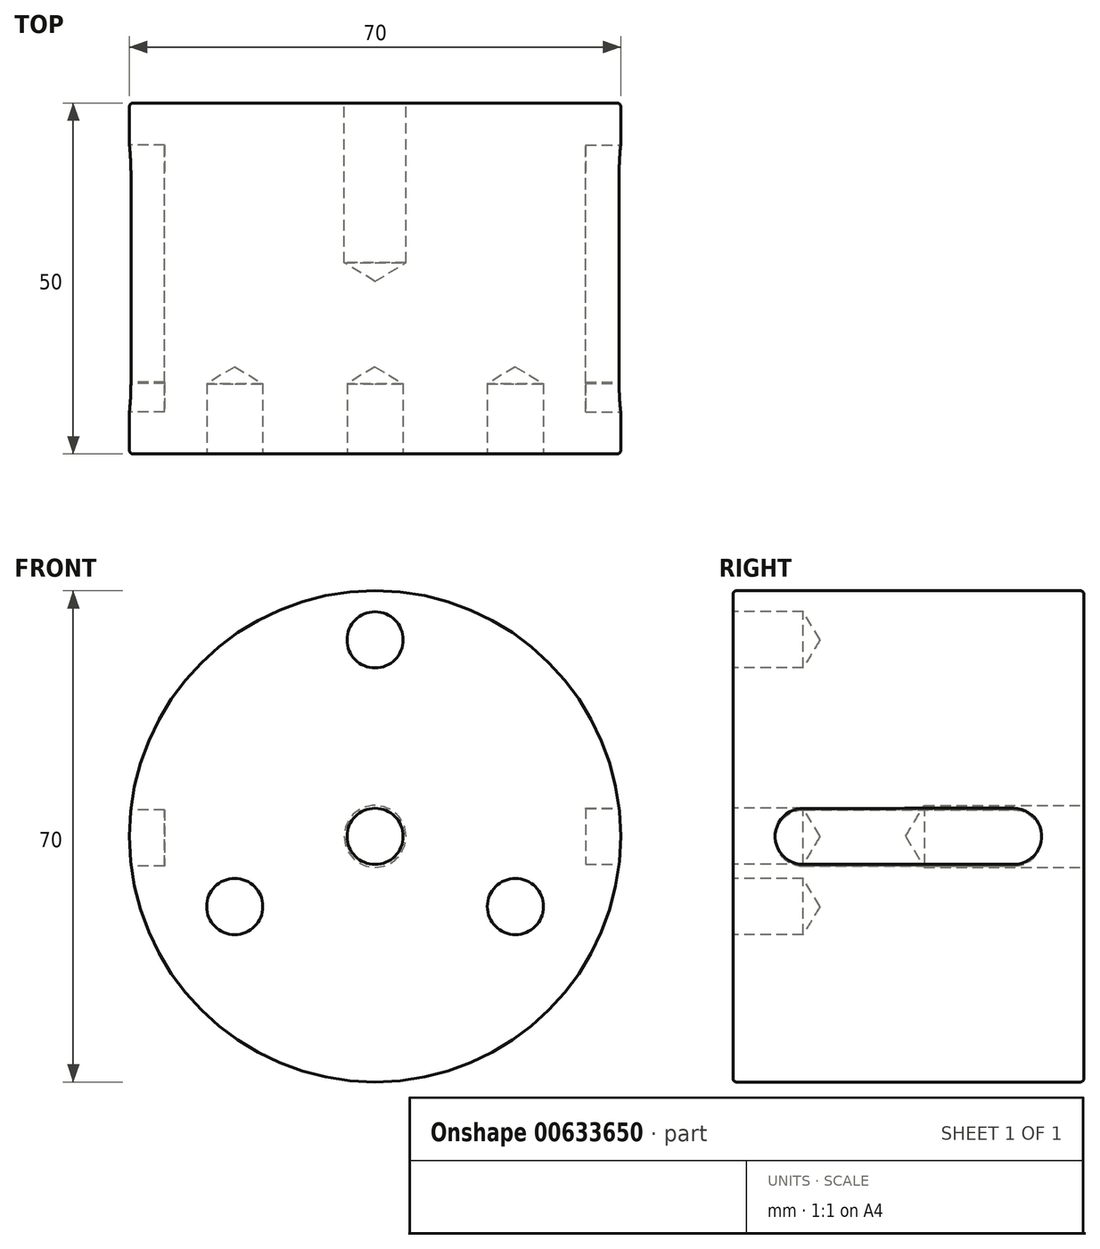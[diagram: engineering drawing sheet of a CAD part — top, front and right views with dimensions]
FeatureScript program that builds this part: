
annotation { "Feature Type Name" : "Feature", "Feature Type Description" : "" }
export const myFeature = defineFeature(function(context is Context, id is Id, definition is map)
    precondition{}
    {
        {
            var Q0;
            Q0=qCreatedBy(makeId("Front.planeOp"),FACE);
            var sketch = newSketch(context, id + "F0", { "sketchPlane" : qUnion([Q0])});
            skCircle(sketch, "E0", {"center": v(0, 0) * mm, "radius": 35 * mm});
            skSolve(sketch);
        }
        {
            var Q0;
            Q0=makeQuery(id+"F0.imprint","IMPRINT",FACE,{"disambiguationData":[TD([[makeQuery(id+"F0.imprint","IMPRINT",EDGE,{"derivedFrom":sQuery(id+"F0.wireOp",EDGE,"E0")}),1.0]])]});
            extrude(context, id + "F1", {"entities" : qUnion([Q0]), "depth" : 50 * mm, "offsetDistance" : 25 * mm});
        }
        {
            var Q0;
            Q0=makeQuery(id+"F1.opExtrude","CAP_FACE",FACE,{"disambiguationData":[OSD([sQuery(id+"F0.wireOp",EDGE,"E0")])],"isStart":false});
            var sketch = newSketch(context, id + "F2", { "sketchPlane" : qUnion([Q0])});
            skPoint(sketch, "E1", {"position": v(0, 28) * mm});
            skPoint(sketch, "E2", {"position": v(0, 0) * mm});
            skPoint(sketch, "E3", {"position": v(-20, -10) * mm});
            skPoint(sketch, "E4", {"position": v(20, -10) * mm});
            skSolve(sketch);
        }
        {
            var Q0;
            Q0=sQuery(id+"F2.wireOp",VERTEX,"E1");
            var Q1;
            Q1=sQuery(id+"F2.wireOp",VERTEX,"E2");
            var Q2;
            Q2=sQuery(id+"F2.wireOp",VERTEX,"E4");
            var Q3;
            Q3=sQuery(id+"F2.wireOp",VERTEX,"E3");
            var Q4;
            Q4=makeQuery(id+"F1.opExtrude","SWEPT_BODY",BODY,{"disambiguationData":[OSD([sQuery(id+"F0.wireOp",EDGE,"E0")])]});
            hole(context, id + "F3", {"style" : HoleStyle.SIMPLE, "endStyle" : HoleEndStyle.BLIND, "holeDiameter" : 8 * mm, "majorDiameter" : 12 * mm, "holeDepth" : 10 * mm, "isTappedThrough" : true, "tappedDepth" : 8 * mm, "tapClearance" : 3, "startFromSketch" : true, "locations" : qUnion([Q0, Q1, Q2, Q3]), "scope" : qUnion([Q4])});
        }
        {
            var Q0;
            Q0=qCreatedBy(makeId("Right.planeOp"),FACE);
            cPlane(context, id + "F4", {"entities" : qUnion([Q0]), "cplaneType" : CPlaneType.OFFSET, "offset" : 35 * mm, "width" : 150 * mm, "height" : 150 * mm});
        }
        {
            var Q0;
            Q0=qCreatedBy(id+"F4.planeOp",FACE);
            var sketch = newSketch(context, id + "F5", { "sketchPlane" : qUnion([Q0])});
            skPoint(sketch, "E5", {"position": v(-40, 0) * mm});
            skPoint(sketch, "E6", {"position": v(-10, 0) * mm});
            skArc(sketch, "E7", {"start": v(-39.76, 4) * mm, "mid": v(-44, 0.1) * mm, "end": v(-39.95, -4) * mm});
            skArc(sketch, "E8", {"start": v(-10, -4) * mm, "mid": v(-6, 0) * mm, "end": v(-10, 4) * mm});
            skLineSegment(sketch, "E9", {"start": v(-39.95, -4) * mm, "end": v(-10, -4) * mm});
            skLineSegment(sketch, "E10", {"start": v(-39.76, 4) * mm, "end": v(-10, 4) * mm});
            skSolve(sketch);
        }
        {
            var Q0;
            Q0 = qSketchRegion(id + "F5", true);
            var Q1;
            Q1=makeQuery(id+"F5.imprint","IMPRINT",FACE,{"disambiguationData":[TD([[makeQuery(id+"F5.imprint","IMPRINT",EDGE,{"derivedFrom":sQuery(id+"F5.wireOp",EDGE,"E7")}),1.0]])]});
            extrude(context, id + "F6", {"entities" : qUnion([Q0, Q1]), "operationType" : NewBodyOperationType.REMOVE, "oppositeDirection" : true, "depth" : 5 * mm, "offsetDistance" : 25 * mm});
        }
        {
            var Q0;
            Q0=qCreatedBy(makeId("Right.planeOp"),FACE);
            cPlane(context, id + "F7", {"entities" : qUnion([Q0]), "cplaneType" : CPlaneType.OFFSET, "offset" : 35 * mm, "oppositeDirection" : true, "width" : 150 * mm, "height" : 150 * mm});
        }
        {
            var Q0;
            Q0=qCreatedBy(id+"F7.planeOp",FACE);
            var sketch = newSketch(context, id + "F8", { "sketchPlane" : qUnion([Q0])});
            skPoint(sketch, "E11", {"position": v(-10, 0) * mm});
            skPoint(sketch, "E12", {"position": v(-40, -0.23) * mm});
            skPoint(sketch, "E13", {"position": v(-10, -0.22) * mm});
            skArc(sketch, "E14", {"start": v(-39.76, 3.76) * mm, "mid": v(-44, -0.14) * mm, "end": v(-39.95, -4.23) * mm});
            skArc(sketch, "E15", {"start": v(-10, -4.22) * mm, "mid": v(-6, -0.22) * mm, "end": v(-10, 3.78) * mm});
            skLineSegment(sketch, "E16", {"start": v(-39.95, -4.23) * mm, "end": v(-10, -4.22) * mm});
            skLineSegment(sketch, "E17", {"start": v(-39.76, 3.76) * mm, "end": v(-10, 3.78) * mm});
            skSolve(sketch);
        }
        {
            var Q0;
            Q0=makeQuery(id+"F8.imprint","IMPRINT",FACE,{"disambiguationData":[TD([[makeQuery(id+"F8.imprint","IMPRINT",EDGE,{"derivedFrom":sQuery(id+"F8.wireOp",EDGE,"E14")}),1.0]])]});
            extrude(context, id + "F9", {"entities" : qUnion([Q0]), "operationType" : NewBodyOperationType.REMOVE, "depth" : 5 * mm, "offsetDistance" : 25 * mm});
        }
        {
            var Q0;
            Q0=qCreatedBy(makeId("Front.planeOp"),FACE);
            var sketch = newSketch(context, id + "F10", { "sketchPlane" : qUnion([Q0])});
            skPoint(sketch, "E18", {"position": v(0, 0) * mm});
            skSolve(sketch);
        }
        {
            var Q0;
            Q0=sQuery(id+"F10.wireOp",VERTEX,"E18");
            var Q1;
            Q1=makeQuery(id+"F1.opExtrude","SWEPT_BODY",BODY,{"disambiguationData":[OSD([sQuery(id+"F0.wireOp",EDGE,"E0")])]});
            hole(context, id + "F11", {"style" : HoleStyle.SIMPLE, "endStyle" : HoleEndStyle.BLIND, "oppositeDirection" : true, "standardTappedOrClearance" : lookupTablePath({ "standard" : "ISO", "engagement" : "75%", "pitch" : "1.25 mm", "size" : "M10", "type" : "Tapped" }), "standardBlindInLast" : lookupTablePath({ "standard" : "ISO", "engagement" : "75%", "pitch" : "1.25 mm", "size" : "M10", "type" : "Tapped" }), "holeDiameter" : 8.8 * mm, "majorDiameter" : 10 * mm, "showTappedDepth" : true, "holeDepth" : 22.75 * mm, "isTappedThrough" : true, "tappedDepth" : 19 * mm, "tapClearance" : 3, "locations" : qUnion([Q0]), "scope" : qUnion([Q1])});
        }
        {
            var Q0;
            Q0=makeQuery(id+"F1.opExtrude","CAP_EDGE",EDGE,{"disambiguationData":[OSD([sQuery(id+"F0.wireOp",EDGE,"E0")])],"isStart":false});
            var Q1;
            Q1=makeQuery(id+"F1.opExtrude","CAP_EDGE",EDGE,{"disambiguationData":[OSD([sQuery(id+"F0.wireOp",EDGE,"E0")])],"isStart":true});
            fillet(context, id + "F12", {"entities" : qUnion([Q0, Q1]), "radius" : .5 * mm, "tangentPropagation" : true, "allowEdgeOverflow" : false});
        }
    });
